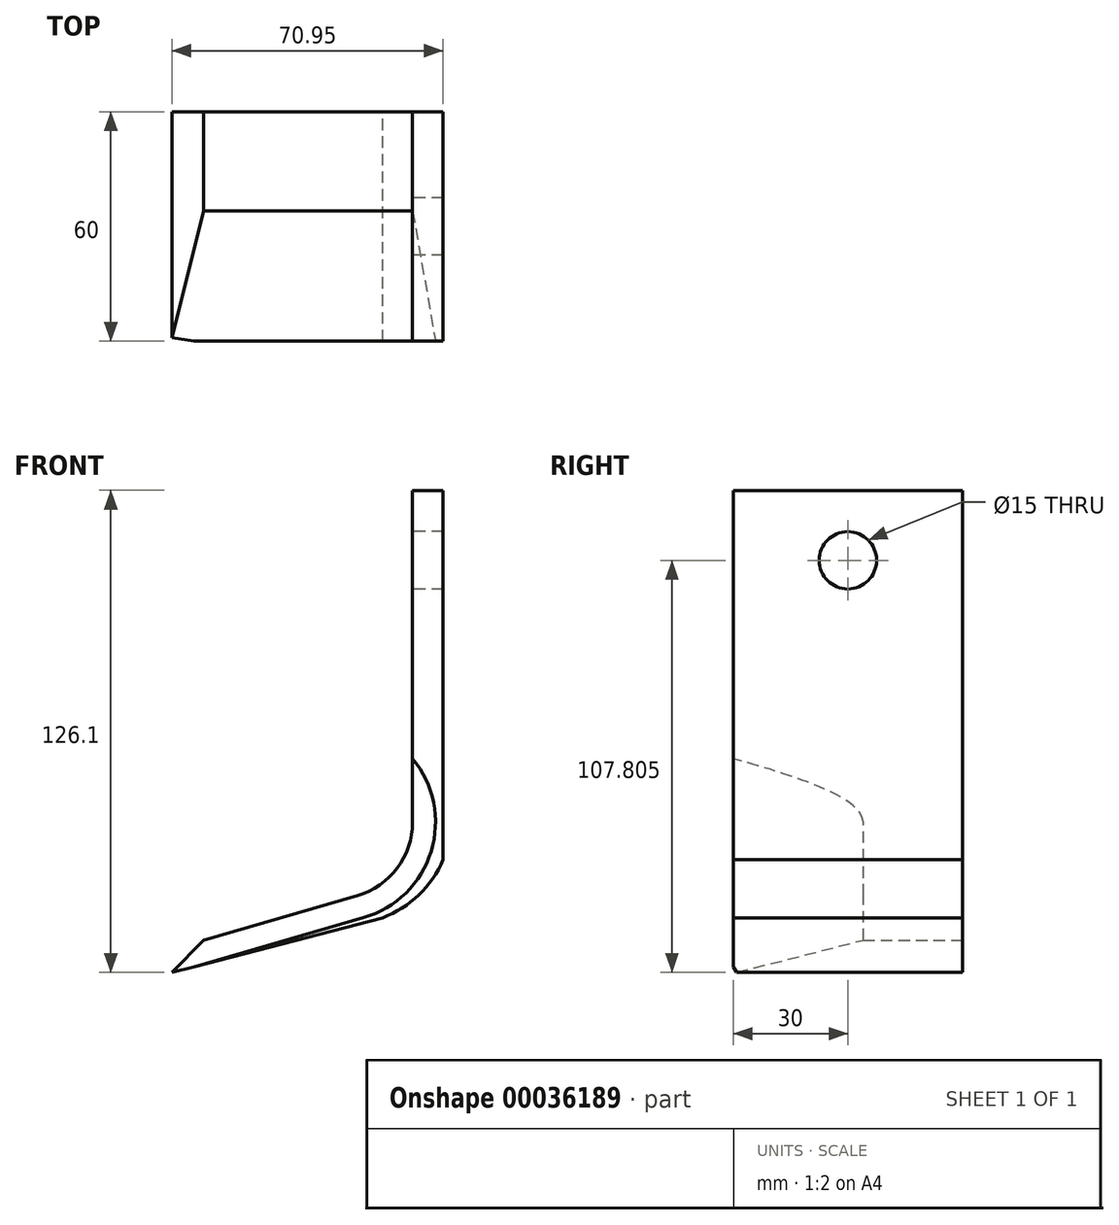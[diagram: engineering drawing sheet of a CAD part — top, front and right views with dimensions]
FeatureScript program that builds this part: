
annotation { "Feature Type Name" : "Feature", "Feature Type Description" : "" }
export const myFeature = defineFeature(function(context is Context, id is Id, definition is map)
    precondition{}
    {
        {
            var Q0;
            Q0=qCreatedBy(makeId("Front.planeOp"),FACE);
            var sketch = newSketch(context, id + "F0", { "sketchPlane" : qUnion([Q0])});
            skLineSegment(sketch, "E0.left", {"start": v(7.87, 46.78) * mm, "end": v(7.87, -40) * mm});
            skLineSegment(sketch, "E1", {"start": v(15.87, -40) * mm, "end": v(15.87, -49.85) * mm});
            skLineSegment(sketch, "E2", {"start": v(15.87, 46.78) * mm, "end": v(15.87, -49.85) * mm});
            skLineSegment(sketch, "E3", {"start": v(7.87, 46.78) * mm, "end": v(15.87, 46.78) * mm});
            skArc(sketch, "E4", {"start": v(-6.58, -59.22) * mm, "mid": v(3.85, -52.02) * mm, "end": v(7.87, -40) * mm});
            skLineSegment(sketch, "E5", {"start": v(-6.58, -59.22) * mm, "end": v(-46.78, -70.83) * mm});
            skLineSegment(sketch, "E6", {"start": v(-46.78, -70.83) * mm, "end": v(-55.08, -79.32) * mm});
            skArc(sketch, "E7", {"start": v(0, -64.99) * mm, "mid": v(9.48, -59.04) * mm, "end": v(15.87, -49.85) * mm});
            skLineSegment(sketch, "E8", {"start": v(0, -64.99) * mm, "end": v(-55.08, -79.32) * mm});
            skSolve(sketch);
        }
        {
            var Q0;
            Q0=makeQuery(id+"F0.imprint","IMPRINT",FACE,{"disambiguationData":[TD([[makeQuery(id+"F0.imprint","IMPRINT",EDGE,{"derivedFrom":sQuery(id+"F0.wireOp",EDGE,"E0.left")}),1.0]])]});
            extrude(context, id + "F1", {"entities" : qUnion([Q0]), "depth" : 60 * mm});
        }
        {
            var Q0;
            Q0=makeQuery(id+"F1.opExtrude","CAP_EDGE",EDGE,{"disambiguationData":[OSD([sQuery(id+"F0.wireOp",EDGE,"E5")])],"isStart":false});
            var Q1;
            Q1=makeQuery(id+"F1.opExtrude","CAP_EDGE",EDGE,{"disambiguationData":[OSD([sQuery(id+"F0.wireOp",EDGE,"E4")])],"isStart":false});
            chamfer(context, id + "F2", {"entities" : qUnion([Q0, Q1]), "chamferType" : ChamferType.OFFSET_ANGLE, "width" : 6 * mm, "oppositeDirection" : false, "angle" : 80 * degree});
        }
        {
            var Q0;
            Q0=makeQuery(id+"F1.opExtrude","SWEPT_FACE",FACE,{"disambiguationData":[OSD([sQuery(id+"F0.wireOp",EDGE,"E0.left")])]});
            var sketch = newSketch(context, id + "F3", { "sketchPlane" : qUnion([Q0])});
            skCircle(sketch, "E9", {"center": v(30, 28.48) * mm, "radius": 7.5 * mm});
            skPoint(sketch, "E9.centerSnap0", {"position": v(30, 46.78) * mm});
            skSolve(sketch);
        }
        {
            var Q0;
            Q0=makeQuery(id+"F3.imprint","IMPRINT",FACE,{"disambiguationData":[TD([[makeQuery(id+"F3.imprint","IMPRINT",EDGE,{"derivedFrom":sQuery(id+"F3.wireOp",EDGE,"E9")}),1.0]])]});
            extrude(context, id + "F4", {"entities" : qUnion([Q0]), "operationType" : NewBodyOperationType.REMOVE, "oppositeDirection" : true, "depth" : 25 * mm});
        }
    });
